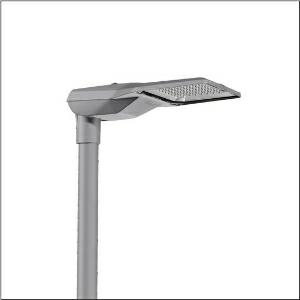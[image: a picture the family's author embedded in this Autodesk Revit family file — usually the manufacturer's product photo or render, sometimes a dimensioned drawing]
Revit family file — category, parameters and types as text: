
# Revit family: streetlight_sl_21_midi___st1_0a_5xe3d33s08mb_8b67
name_source: partatom
category: Lighting Fixtures
units: mm (PartAtom-declared; Revit-internal decimal feet)

## family parameters
Cut with Voids When Loaded = No
Host = Face
Light Source = No
Part Type = Normal
Room Calculation Point = No
Round Connector Dimension = Use Diameter
Shared = No

## types (1)
- --- (1 x LED, 18270 lm, 136 W, 3000K)
    Apparent Load = 136 VA
    CIE Flux Codes = 37 72 97 100 100
    Color Rendering = 70
    Color Temperature = 3000K
    Default Elevation = 1800 mm
    Description = Streetlight SL 21 midi, mast luminaire, primary light control with lens, of PMMA, primary optical cover: cover, of toughened safety glass, transparent, light distribution: ST1.0a, light emission: direct distribution, primary light characteristic: asymmetric, installation type: side-entry, post-top, LED, High Power LED, rated luminous flux: 18.270lm, luminous efficacy: 134lm/W, light colour: 730, colour temperature: 3000K, control gear: D4i, control: flexible luminous flux parameterisation, time-dependent luminous flux control, constant luminous flux control, overheat protection, pre-setting: logarithmic dimming characteristic, mains connection: 230..240V, AC, 50/60Hz, start of lifetime: 136W, end of service life: 142W, reduction: 61W, luminaire housing, of diecast aluminium, powder-coated, SITECO metallic grey (DB 702S), corrosivity category C5 high according to DIN EN ISO 12944, please order mast flange separately, inclination adjustable: 0°, 5°, 10°, 15°, sealing non-destructively replaceable, multi-level sealing system, length: 644mm, width: 335mm, height: 110mm, mast flange for spigot size: 42mm (side-entry): 5XC10008XM4, 60/48mm (side-entry/post-top): 5XC10108XM2, 76/60mm (side-entry/post-top): 5XC10108XM1, mounting height: 4..8m, Smart Interface above, protection rating (complete): IP66, insulation class (complete): insulation class II (safety insulation), certification: CE, ENEC, ENEC+, VDE, impact resistance: IK10, permissible operating ambient temperature for outdoor applications: -40..+50°C, standard-compliant lighting for roads and squares, packaging unit: 1 piece

Light Distribution: ST1.0a
    Height = 111 mm
    Lamp = 1 x LED
    Lamp Light Flux = 18270 lm
    Lamp Power = 136 W
    Lamp count = 1
    Length = 644 mm
    Luminous efficacy = 134 lm/W
    Manufacturer = Siteco
    ModVariant = No
    Model = 5XE3D33S08MB
    Number of Poles = 1
    OnlyDefault = Yes
    Power Factor = 1
    Product Name = Streetlight SL 21 midi | ST1.0a
    Product group = mast luminaire | pylon top
    ProductGroupID = 6100
    Protection Class = Protection class II
    Protection Degree = IP 66
    RLX_Detail_Level = 1
    RLX_Emergency_Light_Flux = 0 lm
    RLX_Emergency_Type = 0
    RLX_Emergency_Type_DB = No
    RlxData = <blob elided: 26801 chars, md5=70f2e828>
    Socket = socket
    Standby Power = 0 W
    System Light Flux = 18270 lm
    System Power = 136 W
    Type Comments = factory setting: luminous flux: 100 % | dim-lin: 254 | 695 mA
    Type Image = l_1004302.jpg
    URL = http://relux.com
    VarID = @adj_186807
    Voltage = 0 V
    Weight = 0.00 kg
    Width = 336 mm

## geometry (parser evidence)
native form markers: Blend x4, Sweep x10
no freeform markers — native parametric forms only
